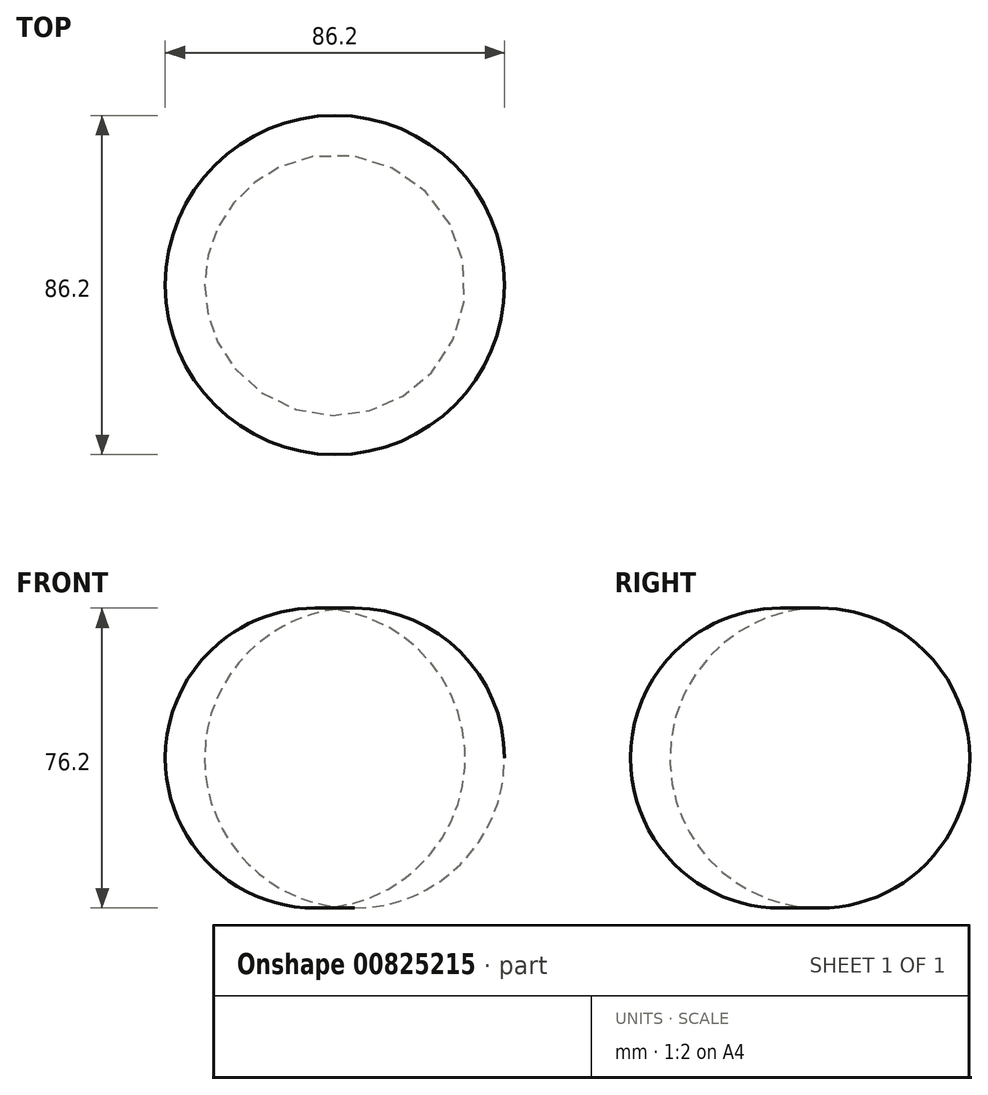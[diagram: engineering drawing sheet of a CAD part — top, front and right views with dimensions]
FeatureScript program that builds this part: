
annotation { "Feature Type Name" : "Feature", "Feature Type Description" : "" }
export const myFeature = defineFeature(function(context is Context, id is Id, definition is map)
    precondition{}
    {
        {
            var Q0;
            Q0=qCreatedBy(makeId("Front.planeOp"),FACE);
            var sketch = newSketch(context, id + "F0", { "sketchPlane" : qUnion([Q0])});
            skLineSegment(sketch, "E0", {"start": v(0, 75.54) * mm, "end": v(0, 0) * mm});
            skArc(sketch, "E1", {"start": v(0, 0) * mm, "mid": v(33.1, 37.77) * mm, "end": v(0, 75.54) * mm});
            skSolve(sketch);
        }
        {
            var Q0;
            Q0 = qSketchRegion(id + "F0", true);
            var Q1;
            Q1=sQuery(id+"F0.wireOp",EDGE,"E0");
            revolve(context, id + "F1", {"surfaceOperationType" : NewSurfaceOperationType.NEW, "entities" : qUnion([Q0]), "axis" : qUnion([Q1]), "revolveType" : RevolveType.FULL});
        }
    });
